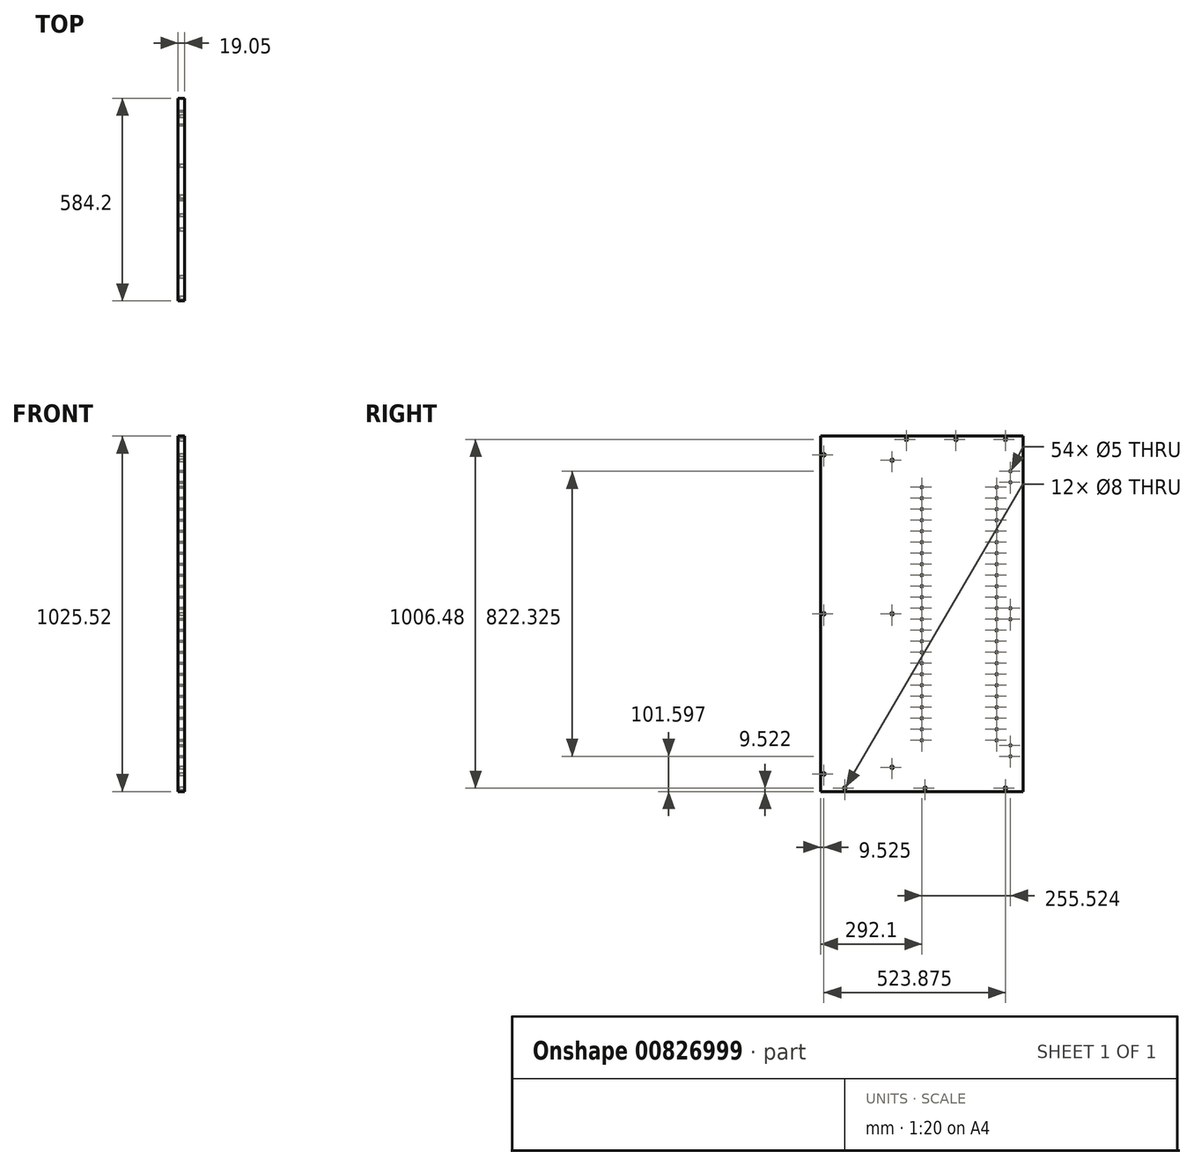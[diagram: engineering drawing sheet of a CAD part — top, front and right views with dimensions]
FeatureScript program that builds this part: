
annotation { "Feature Type Name" : "Feature", "Feature Type Description" : "" }
export const myFeature = defineFeature(function(context is Context, id is Id, definition is map)
    precondition{}
    {
        {
            var Q0;
            Q0=qCreatedBy(makeId("Right.planeOp"),FACE);
            var sketch = newSketch(context, id + "F0", { "sketchPlane" : qUnion([Q0])});
            skLineSegment(sketch, "E0.bottom", {"start": v(292.1, 512.76) * mm, "end": v(-292.1, 512.76) * mm});
            skLineSegment(sketch, "E0.top", {"start": v(292.1, -512.76) * mm, "end": v(-292.1, -512.76) * mm});
            skLineSegment(sketch, "E0.left", {"start": v(292.1, 512.76) * mm, "end": v(292.1, -512.76) * mm});
            skLineSegment(sketch, "E0.right", {"start": v(-292.1, 512.76) * mm, "end": v(-292.1, -512.76) * mm});
            skPoint(sketch, "E0.middle", {"position": v(0, 0) * mm});
            skSolve(sketch);
        }
        {
            var Q0;
            Q0=makeQuery(id+"F0.imprint","IMPRINT",FACE,{"disambiguationData":[TD([[makeQuery(id+"F0.imprint","IMPRINT",EDGE,{"derivedFrom":sQuery(id+"F0.wireOp",EDGE,"E0.bottom")}),1.0]])]});
            extrude(context, id + "F1", {"entities" : qUnion([Q0]), "depth" : 19.05 * mm, "offsetDistance" : 25.4 * mm});
        }
        {
            var Q0;
            Q0=makeQuery(id+"F1.opExtrude","CAP_FACE",FACE,{"disambiguationData":[OSD([sQuery(id+"F0.wireOp",EDGE,"E0.bottom"),sQuery(id+"F0.wireOp",EDGE,"E0.top"),sQuery(id+"F0.wireOp",EDGE,"E0.left"),sQuery(id+"F0.wireOp",EDGE,"E0.right")])],"isStart":false});
            var sketch = newSketch(context, id + "F2", { "sketchPlane" : qUnion([Q0])});
            skLineSegment(sketch, "E1.bottom", {"start": v(-292.1, -512.76) * mm, "end": v(273.05, -512.76) * mm});
            skLineSegment(sketch, "E1.top", {"start": v(-292.1, -493.71) * mm, "end": v(273.05, -493.71) * mm});
            skLineSegment(sketch, "E1.left", {"start": v(-292.1, -512.76) * mm, "end": v(-292.1, -493.71) * mm});
            skLineSegment(sketch, "E1.right", {"start": v(273.05, -512.76) * mm, "end": v(273.05, -493.71) * mm});
            skLineSegment(sketch, "E2", {"start": v(-292.1, -503.24) * mm, "end": v(-241.3, -503.24) * mm});
            skLineSegment(sketch, "E3", {"start": v(273.05, -503.24) * mm, "end": v(222.25, -503.24) * mm});
            skLineSegment(sketch, "E4", {"start": v(-9.53, -493.71) * mm, "end": v(-9.53, -512.76) * mm});
            skPoint(sketch, "E5", {"position": v(-241.3, -503.24) * mm});
            skPoint(sketch, "E6", {"position": v(-9.53, -503.24) * mm});
            skPoint(sketch, "E7", {"position": v(222.25, -503.24) * mm});
            skLineSegment(sketch, "E8", {"start": v(292.1, 512.76) * mm, "end": v(292.1, 509.59) * mm});
            skLineSegment(sketch, "E9.bottom", {"start": v(292.1, 509.59) * mm, "end": v(273.05, 509.59) * mm});
            skLineSegment(sketch, "E9.top", {"start": v(292.1, -512.76) * mm, "end": v(273.05, -512.76) * mm});
            skLineSegment(sketch, "E9.left", {"start": v(292.1, 509.59) * mm, "end": v(292.1, -512.76) * mm});
            skLineSegment(sketch, "E9.right", {"start": v(273.05, 509.59) * mm, "end": v(273.05, -512.76) * mm});
            skLineSegment(sketch, "E10", {"start": v(282.58, -512.76) * mm, "end": v(282.58, -461.96) * mm});
            skLineSegment(sketch, "E11", {"start": v(282.58, 509.59) * mm, "end": v(282.58, 458.79) * mm});
            skLineSegment(sketch, "E12", {"start": v(273.05, 0) * mm, "end": v(282.58, 0) * mm});
            skPoint(sketch, "E13", {"position": v(282.58, 0) * mm});
            skPoint(sketch, "E14", {"position": v(282.58, 458.79) * mm});
            skPoint(sketch, "E15", {"position": v(282.58, -461.96) * mm});
            skLineSegment(sketch, "E16.bottom", {"start": v(-292.1, 512.76) * mm, "end": v(95.25, 512.76) * mm});
            skLineSegment(sketch, "E16.top", {"start": v(-292.1, 493.71) * mm, "end": v(95.25, 493.71) * mm});
            skLineSegment(sketch, "E16.left", {"start": v(-292.1, 512.76) * mm, "end": v(-292.1, 493.71) * mm});
            skLineSegment(sketch, "E16.right", {"start": v(95.25, 512.76) * mm, "end": v(95.25, 493.71) * mm});
            skLineSegment(sketch, "E17", {"start": v(-292.1, 503.24) * mm, "end": v(-241.3, 503.24) * mm});
            skLineSegment(sketch, "E18", {"start": v(95.25, 503.24) * mm, "end": v(44.45, 503.24) * mm});
            skLineSegment(sketch, "E19", {"start": v(-98.43, 493.71) * mm, "end": v(-98.43, 512.76) * mm});
            skPoint(sketch, "E20", {"position": v(-241.3, 503.24) * mm});
            skPoint(sketch, "E21", {"position": v(-98.43, 503.24) * mm});
            skPoint(sketch, "E22", {"position": v(44.45, 503.24) * mm});
            skLineSegment(sketch, "E23.bottom", {"start": v(95.25, 493.71) * mm, "end": v(76.2, 493.71) * mm});
            skLineSegment(sketch, "E23.top", {"start": v(95.25, -493.71) * mm, "end": v(76.2, -493.71) * mm});
            skLineSegment(sketch, "E23.left", {"start": v(95.25, 493.71) * mm, "end": v(95.25, -493.71) * mm});
            skLineSegment(sketch, "E23.right", {"start": v(76.2, 493.71) * mm, "end": v(76.2, -493.71) * mm});
            skLineSegment(sketch, "E24", {"start": v(85.72, 493.71) * mm, "end": v(85.72, 442.91) * mm});
            skLineSegment(sketch, "E25", {"start": v(85.72, -493.71) * mm, "end": v(85.72, -442.91) * mm});
            skPoint(sketch, "E26", {"position": v(85.72, 442.91) * mm});
            skPoint(sketch, "E27", {"position": v(85.72, -442.91) * mm});
            skPoint(sketch, "E28", {"position": v(85.72, 0) * mm});
            skPoint(sketch, "E28.positionSnap0", {"position": v(95.25, 0) * mm});
            skSolve(sketch);
        }
        {
            var Q0;
            Q0=sQuery(id+"F2.wireOp",VERTEX,"E20");
            var Q1;
            Q1=sQuery(id+"F2.wireOp",VERTEX,"E21");
            var Q2;
            Q2=sQuery(id+"F2.wireOp",VERTEX,"E22");
            var Q3;
            Q3=sQuery(id+"F2.wireOp",VERTEX,"E26");
            var Q4;
            Q4=sQuery(id+"F2.wireOp",VERTEX,"E14");
            var Q5;
            Q5=sQuery(id+"F2.wireOp",VERTEX,"E13");
            var Q6;
            Q6=sQuery(id+"F2.wireOp",VERTEX,"E28");
            var Q7;
            Q7=sQuery(id+"F2.wireOp",VERTEX,"E15");
            var Q8;
            Q8=sQuery(id+"F2.wireOp",VERTEX,"E7");
            var Q9;
            Q9=sQuery(id+"F2.wireOp",VERTEX,"E27");
            var Q10;
            Q10=sQuery(id+"F2.wireOp",VERTEX,"E6");
            var Q11;
            Q11=sQuery(id+"F2.wireOp",VERTEX,"E5");
            var Q12;
            Q12=makeQuery(id+"F1.opExtrude","SWEPT_BODY",BODY,{"disambiguationData":[OSD([sQuery(id+"F0.wireOp",EDGE,"E0.bottom"),sQuery(id+"F0.wireOp",EDGE,"E0.top"),sQuery(id+"F0.wireOp",EDGE,"E0.left"),sQuery(id+"F0.wireOp",EDGE,"E0.right")])]});
            hole(context, id + "F3", {"style" : HoleStyle.SIMPLE, "endStyle" : HoleEndStyle.BLIND, "holeDiameter" : 8 * mm, "majorDiameter" : 6.35 * mm, "holeDepth" : 14.22 * mm, "isTappedThrough" : true, "tappedDepth" : 12.7 * mm, "tapClearance" : 3, "startFromSketch" : true, "locations" : qUnion([Q0, Q1, Q2, Q3, Q4, Q5, Q6, Q7, Q8, Q9, Q10, Q11]), "scope" : qUnion([Q12])});
        }
        {
            var Q0;
            Q0=makeQuery(id+"F1.opExtrude","CAP_FACE",FACE,{"disambiguationData":[OSD([sQuery(id+"F0.wireOp",EDGE,"E0.bottom"),sQuery(id+"F0.wireOp",EDGE,"E0.top"),sQuery(id+"F0.wireOp",EDGE,"E0.left"),sQuery(id+"F0.wireOp",EDGE,"E0.right")])],"isStart":false});
            var sketch = newSketch(context, id + "F4", { "sketchPlane" : qUnion([Q0])});
            skLineSegment(sketch, "E29", {"start": v(-292.1, 512.76) * mm, "end": v(-292.1, 411.16) * mm});
            skLineSegment(sketch, "E30", {"start": v(-292.1, 411.16) * mm, "end": v(-255.52, 411.16) * mm});
            skLineSegment(sketch, "E31", {"start": v(-292.1, -512.76) * mm, "end": v(-292.1, -411.16) * mm});
            skLineSegment(sketch, "E32", {"start": v(-292.1, -411.16) * mm, "end": v(-255.52, -411.16) * mm});
            skLineSegment(sketch, "E33", {"start": v(-255.52, -411.16) * mm, "end": v(-255.52, -379.41) * mm});
            skLineSegment(sketch, "E34", {"start": v(-255.52, 411.16) * mm, "end": v(-255.52, 379.41) * mm});
            skLineSegment(sketch, "E35", {"start": v(-292.1, 0) * mm, "end": v(-255.52, 0) * mm});
            skLineSegment(sketch, "E36", {"start": v(-255.52, 0) * mm, "end": v(-255.52, 15.88) * mm});
            skLineSegment(sketch, "E37", {"start": v(-255.52, 0) * mm, "end": v(-255.52, -15.88) * mm});
            skPoint(sketch, "E38", {"position": v(-255.52, 411.16) * mm});
            skPoint(sketch, "E39", {"position": v(-255.52, 379.41) * mm});
            skPoint(sketch, "E40", {"position": v(-255.52, 15.88) * mm});
            skPoint(sketch, "E41", {"position": v(-255.52, -15.88) * mm});
            skPoint(sketch, "E42", {"position": v(-255.52, -379.41) * mm});
            skPoint(sketch, "E43", {"position": v(-255.52, -411.16) * mm});
            skLineSegment(sketch, "E44", {"start": v(-292.1, 512.76) * mm, "end": v(-215.9, 512.76) * mm});
            skLineSegment(sketch, "E45", {"start": v(-215.9, 512.76) * mm, "end": v(-215.9, 365.19) * mm});
            skLineSegment(sketch, "E46", {"start": v(-292.1, 512.76) * mm, "end": v(0, 512.76) * mm});
            skLineSegment(sketch, "E47.bottom", {"start": v(-215.9, 365.19) * mm, "end": v(0, 365.19) * mm});
            skLineSegment(sketch, "E47.top", {"start": v(-215.9, 301.69) * mm, "end": v(0, 301.69) * mm});
            skLineSegment(sketch, "E47.left", {"start": v(-215.9, 365.19) * mm, "end": v(-215.9, 301.69) * mm});
            skLineSegment(sketch, "E47.right", {"start": v(0, 365.19) * mm, "end": v(0, 301.69) * mm});
            skLineSegment(sketch, "E48", {"start": v(-215.9, 301.69) * mm, "end": v(-215.9, 269.94) * mm});
            skLineSegment(sketch, "E49.bottom", {"start": v(-215.9, 269.94) * mm, "end": v(0, 269.94) * mm});
            skLineSegment(sketch, "E49.top", {"start": v(-215.9, 206.44) * mm, "end": v(0, 206.44) * mm});
            skLineSegment(sketch, "E49.left", {"start": v(-215.9, 269.94) * mm, "end": v(-215.9, 206.44) * mm});
            skLineSegment(sketch, "E49.right", {"start": v(0, 269.94) * mm, "end": v(0, 206.44) * mm});
            skLineSegment(sketch, "E50", {"start": v(-215.9, 206.44) * mm, "end": v(-215.9, 174.69) * mm});
            skLineSegment(sketch, "E51.bottom", {"start": v(-215.9, 174.69) * mm, "end": v(0, 174.69) * mm});
            skLineSegment(sketch, "E51.top", {"start": v(-215.9, 111.19) * mm, "end": v(0, 111.19) * mm});
            skLineSegment(sketch, "E51.left", {"start": v(-215.9, 174.69) * mm, "end": v(-215.9, 111.19) * mm});
            skLineSegment(sketch, "E51.right", {"start": v(0, 174.69) * mm, "end": v(0, 111.19) * mm});
            skLineSegment(sketch, "E52", {"start": v(-215.9, 111.19) * mm, "end": v(-215.9, 79.44) * mm});
            skLineSegment(sketch, "E53.bottom", {"start": v(-215.9, 79.44) * mm, "end": v(0, 79.44) * mm});
            skLineSegment(sketch, "E53.top", {"start": v(-215.9, 15.94) * mm, "end": v(0, 15.94) * mm});
            skLineSegment(sketch, "E53.left", {"start": v(-215.9, 79.44) * mm, "end": v(-215.9, 15.94) * mm});
            skLineSegment(sketch, "E53.right", {"start": v(0, 79.44) * mm, "end": v(0, 15.94) * mm});
            skLineSegment(sketch, "E54", {"start": v(-215.9, 15.94) * mm, "end": v(-215.9, -15.81) * mm});
            skLineSegment(sketch, "E55.bottom", {"start": v(-215.9, -15.81) * mm, "end": v(0, -15.81) * mm});
            skLineSegment(sketch, "E55.top", {"start": v(-215.9, -79.31) * mm, "end": v(0, -79.31) * mm});
            skLineSegment(sketch, "E55.left", {"start": v(-215.9, -15.81) * mm, "end": v(-215.9, -79.31) * mm});
            skLineSegment(sketch, "E55.right", {"start": v(0, -15.81) * mm, "end": v(0, -79.31) * mm});
            skLineSegment(sketch, "E56", {"start": v(-215.9, -79.31) * mm, "end": v(-215.9, -111.06) * mm});
            skLineSegment(sketch, "E57.bottom", {"start": v(-215.9, -111.06) * mm, "end": v(0, -111.06) * mm});
            skLineSegment(sketch, "E57.top", {"start": v(-215.9, -174.56) * mm, "end": v(0, -174.56) * mm});
            skLineSegment(sketch, "E57.left", {"start": v(-215.9, -111.06) * mm, "end": v(-215.9, -174.56) * mm});
            skLineSegment(sketch, "E57.right", {"start": v(0, -111.06) * mm, "end": v(0, -174.56) * mm});
            skLineSegment(sketch, "E58", {"start": v(-215.9, -174.56) * mm, "end": v(-215.9, -206.31) * mm});
            skLineSegment(sketch, "E59.bottom", {"start": v(-215.9, -206.31) * mm, "end": v(0, -206.31) * mm});
            skLineSegment(sketch, "E59.top", {"start": v(-215.9, -269.81) * mm, "end": v(0, -269.81) * mm});
            skLineSegment(sketch, "E59.left", {"start": v(-215.9, -206.31) * mm, "end": v(-215.9, -269.81) * mm});
            skLineSegment(sketch, "E59.right", {"start": v(0, -206.31) * mm, "end": v(0, -269.81) * mm});
            skLineSegment(sketch, "E60.bottom", {"start": v(-215.9, -269.81) * mm, "end": v(-215.9, -269.81) * mm});
            skLineSegment(sketch, "E61", {"start": v(-215.9, -269.81) * mm, "end": v(-215.9, -301.56) * mm});
            skLineSegment(sketch, "E62.bottom", {"start": v(-215.9, -301.56) * mm, "end": v(0, -301.56) * mm});
            skLineSegment(sketch, "E62.top", {"start": v(-215.9, -365.06) * mm, "end": v(0, -365.06) * mm});
            skLineSegment(sketch, "E62.left", {"start": v(-215.9, -301.56) * mm, "end": v(-215.9, -365.06) * mm});
            skLineSegment(sketch, "E62.right", {"start": v(0, -301.56) * mm, "end": v(0, -365.06) * mm});
            skPoint(sketch, "E63", {"position": v(-215.9, 365.19) * mm});
            skPoint(sketch, "E64", {"position": v(-215.9, 333.44) * mm});
            skPoint(sketch, "E65", {"position": v(-215.9, 301.69) * mm});
            skPoint(sketch, "E66", {"position": v(-215.9, 269.94) * mm});
            skPoint(sketch, "E67", {"position": v(-215.9, 238.19) * mm});
            skPoint(sketch, "E68", {"position": v(-215.9, 206.44) * mm});
            skPoint(sketch, "E69", {"position": v(-215.9, 174.69) * mm});
            skPoint(sketch, "E70", {"position": v(-215.9, 142.94) * mm});
            skPoint(sketch, "E71", {"position": v(-215.9, 111.19) * mm});
            skPoint(sketch, "E72", {"position": v(-215.9, 79.44) * mm});
            skPoint(sketch, "E73", {"position": v(-215.9, 47.69) * mm});
            skPoint(sketch, "E74", {"position": v(-215.9, 15.94) * mm});
            skPoint(sketch, "E75", {"position": v(-215.9, -15.81) * mm});
            skPoint(sketch, "E76", {"position": v(-215.9, -47.56) * mm});
            skPoint(sketch, "E77", {"position": v(-215.9, -79.31) * mm});
            skPoint(sketch, "E78", {"position": v(-215.9, -111.06) * mm});
            skPoint(sketch, "E79", {"position": v(-215.9, -142.81) * mm});
            skPoint(sketch, "E80", {"position": v(-215.9, -174.56) * mm});
            skPoint(sketch, "E81", {"position": v(-215.9, -206.31) * mm});
            skPoint(sketch, "E82", {"position": v(-215.9, -238.06) * mm});
            skPoint(sketch, "E83", {"position": v(-215.9, -269.81) * mm});
            skPoint(sketch, "E84", {"position": v(-215.9, -301.56) * mm});
            skPoint(sketch, "E85", {"position": v(-215.9, -333.31) * mm});
            skPoint(sketch, "E86", {"position": v(-215.9, -365.06) * mm});
            skPoint(sketch, "E87", {"position": v(0, -333.31) * mm});
            skPoint(sketch, "E88", {"position": v(0, -365.06) * mm});
            skPoint(sketch, "E89", {"position": v(0, -301.56) * mm});
            skPoint(sketch, "E90", {"position": v(0, -269.81) * mm});
            skPoint(sketch, "E91", {"position": v(0, -238.06) * mm});
            skPoint(sketch, "E92", {"position": v(0, -206.31) * mm});
            skPoint(sketch, "E93", {"position": v(0, -174.56) * mm});
            skPoint(sketch, "E94", {"position": v(0, -142.81) * mm});
            skPoint(sketch, "E95", {"position": v(0, -111.06) * mm});
            skPoint(sketch, "E96", {"position": v(0, -79.31) * mm});
            skPoint(sketch, "E97", {"position": v(0, -47.56) * mm});
            skPoint(sketch, "E98", {"position": v(0, -15.81) * mm});
            skPoint(sketch, "E99", {"position": v(0, 15.94) * mm});
            skPoint(sketch, "E100", {"position": v(0, 47.69) * mm});
            skPoint(sketch, "E101", {"position": v(0, 79.44) * mm});
            skPoint(sketch, "E102", {"position": v(0, 111.19) * mm});
            skPoint(sketch, "E103", {"position": v(0, 142.94) * mm});
            skPoint(sketch, "E104", {"position": v(0, 174.69) * mm});
            skPoint(sketch, "E105", {"position": v(0, 206.44) * mm});
            skPoint(sketch, "E106", {"position": v(0, 238.19) * mm});
            skPoint(sketch, "E107", {"position": v(0, 269.94) * mm});
            skPoint(sketch, "E108", {"position": v(0, 365.19) * mm});
            skPoint(sketch, "E109", {"position": v(0, 333.44) * mm});
            skPoint(sketch, "E110", {"position": v(0, 301.69) * mm});
            skSolve(sketch);
        }
        {
            var Q0;
            Q0=sQuery(id+"F4.wireOp",VERTEX,"E38");
            var Q1;
            Q1=sQuery(id+"F4.wireOp",VERTEX,"E39");
            var Q2;
            Q2=sQuery(id+"F4.wireOp",VERTEX,"E40");
            var Q3;
            Q3=sQuery(id+"F4.wireOp",VERTEX,"E41");
            var Q4;
            Q4=sQuery(id+"F4.wireOp",VERTEX,"E42");
            var Q5;
            Q5=sQuery(id+"F4.wireOp",VERTEX,"E43");
            var Q6;
            Q6=sQuery(id+"F4.wireOp",VERTEX,"E63");
            var Q7;
            Q7=sQuery(id+"F4.wireOp",VERTEX,"E65");
            var Q8;
            Q8=sQuery(id+"F4.wireOp",VERTEX,"E66");
            var Q9;
            Q9=sQuery(id+"F4.wireOp",VERTEX,"E68");
            var Q10;
            Q10=sQuery(id+"F4.wireOp",VERTEX,"E69");
            var Q11;
            Q11=sQuery(id+"F4.wireOp",VERTEX,"E71");
            var Q12;
            Q12=sQuery(id+"F4.wireOp",VERTEX,"E72");
            var Q13;
            Q13=sQuery(id+"F4.wireOp",VERTEX,"E73");
            var Q14;
            Q14=sQuery(id+"F4.wireOp",VERTEX,"E74");
            var Q15;
            Q15=sQuery(id+"F4.wireOp",VERTEX,"E75");
            var Q16;
            Q16=sQuery(id+"F4.wireOp",VERTEX,"E76");
            var Q17;
            Q17=sQuery(id+"F4.wireOp",VERTEX,"E77");
            var Q18;
            Q18=sQuery(id+"F4.wireOp",VERTEX,"E78");
            var Q19;
            Q19=sQuery(id+"F4.wireOp",VERTEX,"E79");
            var Q20;
            Q20=sQuery(id+"F4.wireOp",VERTEX,"E80");
            var Q21;
            Q21=sQuery(id+"F4.wireOp",VERTEX,"E81");
            var Q22;
            Q22=sQuery(id+"F4.wireOp",VERTEX,"E82");
            var Q23;
            Q23=sQuery(id+"F4.wireOp",VERTEX,"E83");
            var Q24;
            Q24=sQuery(id+"F4.wireOp",VERTEX,"E85");
            var Q25;
            Q25=sQuery(id+"F4.wireOp",VERTEX,"E86");
            var Q26;
            Q26=sQuery(id+"F4.wireOp",VERTEX,"E84");
            var Q27;
            Q27=sQuery(id+"F4.wireOp",VERTEX,"E88");
            var Q28;
            Q28=sQuery(id+"F4.wireOp",VERTEX,"E89");
            var Q29;
            Q29=sQuery(id+"F4.wireOp",VERTEX,"E90");
            var Q30;
            Q30=sQuery(id+"F4.wireOp",VERTEX,"E92");
            var Q31;
            Q31=sQuery(id+"F4.wireOp",VERTEX,"E93");
            var Q32;
            Q32=sQuery(id+"F4.wireOp",VERTEX,"E94");
            var Q33;
            Q33=sQuery(id+"F4.wireOp",VERTEX,"E95");
            var Q34;
            Q34=sQuery(id+"F4.wireOp",VERTEX,"E96");
            var Q35;
            Q35=sQuery(id+"F4.wireOp",VERTEX,"E98");
            var Q36;
            Q36=sQuery(id+"F4.wireOp",VERTEX,"E99");
            var Q37;
            Q37=sQuery(id+"F4.wireOp",VERTEX,"E101");
            var Q38;
            Q38=sQuery(id+"F4.wireOp",VERTEX,"E102");
            var Q39;
            Q39=sQuery(id+"F4.wireOp",VERTEX,"E104");
            var Q40;
            Q40=sQuery(id+"F4.wireOp",VERTEX,"E105");
            var Q41;
            Q41=sQuery(id+"F4.wireOp",VERTEX,"E107");
            var Q42;
            Q42=sQuery(id+"F4.wireOp",VERTEX,"E110");
            var Q43;
            Q43=sQuery(id+"F4.wireOp",VERTEX,"E108");
            var Q44;
            Q44=sQuery(id+"F4.wireOp",VERTEX,"E64");
            var Q45;
            Q45=sQuery(id+"F4.wireOp",VERTEX,"E109");
            var Q46;
            Q46=sQuery(id+"F4.wireOp",VERTEX,"E106");
            var Q47;
            Q47=sQuery(id+"F4.wireOp",VERTEX,"E67");
            var Q48;
            Q48=sQuery(id+"F4.wireOp",VERTEX,"E70");
            var Q49;
            Q49=sQuery(id+"F4.wireOp",VERTEX,"E103");
            var Q50;
            Q50=sQuery(id+"F4.wireOp",VERTEX,"E100");
            var Q51;
            Q51=sQuery(id+"F4.wireOp",VERTEX,"E97");
            var Q52;
            Q52=sQuery(id+"F4.wireOp",VERTEX,"E91");
            var Q53;
            Q53=sQuery(id+"F4.wireOp",VERTEX,"E87");
            var Q54;
            Q54=makeQuery(id+"F1.opExtrude","SWEPT_BODY",BODY,{"disambiguationData":[OSD([sQuery(id+"F0.wireOp",EDGE,"E0.bottom"),sQuery(id+"F0.wireOp",EDGE,"E0.top"),sQuery(id+"F0.wireOp",EDGE,"E0.left"),sQuery(id+"F0.wireOp",EDGE,"E0.right")])]});
            hole(context, id + "F5", {"style" : HoleStyle.SIMPLE, "endStyle" : HoleEndStyle.BLIND, "holeDiameter" : 5 * mm, "majorDiameter" : 6.35 * mm, "holeDepth" : 14.22 * mm, "isTappedThrough" : true, "tappedDepth" : 12.7 * mm, "tapClearance" : 3, "startFromSketch" : true, "locations" : qUnion([Q0, Q1, Q2, Q3, Q4, Q5, Q6, Q7, Q8, Q9, Q10, Q11, Q12, Q13, Q14, Q15, Q16, Q17, Q18, Q19, Q20, Q21, Q22, Q23, Q24, Q25, Q26, Q27, Q28, Q29, Q30, Q31, Q32, Q33, Q34, Q35, Q36, Q37, Q38, Q39, Q40, Q41, Q42, Q43, Q44, Q45, Q46, Q47, Q48, Q49, Q50, Q51, Q52, Q53]), "scope" : qUnion([Q54])});
        }
        {
            var Q0;
            Q0=makeQuery(id+"F1.opExtrude","SWEPT_BODY",BODY,{"disambiguationData":[OSD([sQuery(id+"F0.wireOp",EDGE,"E0.bottom"),sQuery(id+"F0.wireOp",EDGE,"E0.top"),sQuery(id+"F0.wireOp",EDGE,"E0.left"),sQuery(id+"F0.wireOp",EDGE,"E0.right")])]});
            var Q1;
            Q1=makeQuery(id+"F1.opExtrude","SWEPT_FACE",FACE,{"disambiguationData":[OSD([sQuery(id+"F0.wireOp",EDGE,"E0.left")])]});
            mirror(context, id + "F6", {"entities" : qUnion([Q0]), "mirrorPlane" : qUnion([Q1])});
        }
        {
            var Q0;
            Q0=makeQuery(id+"F1.opExtrude","SWEPT_BODY",BODY,{"disambiguationData":[OSD([sQuery(id+"F0.wireOp",EDGE,"E0.bottom"),sQuery(id+"F0.wireOp",EDGE,"E0.top"),sQuery(id+"F0.wireOp",EDGE,"E0.left"),sQuery(id+"F0.wireOp",EDGE,"E0.right")])]});
            deleteBodies(context, id + "F7", {"entities" : qUnion([Q0])});
        }
    });
